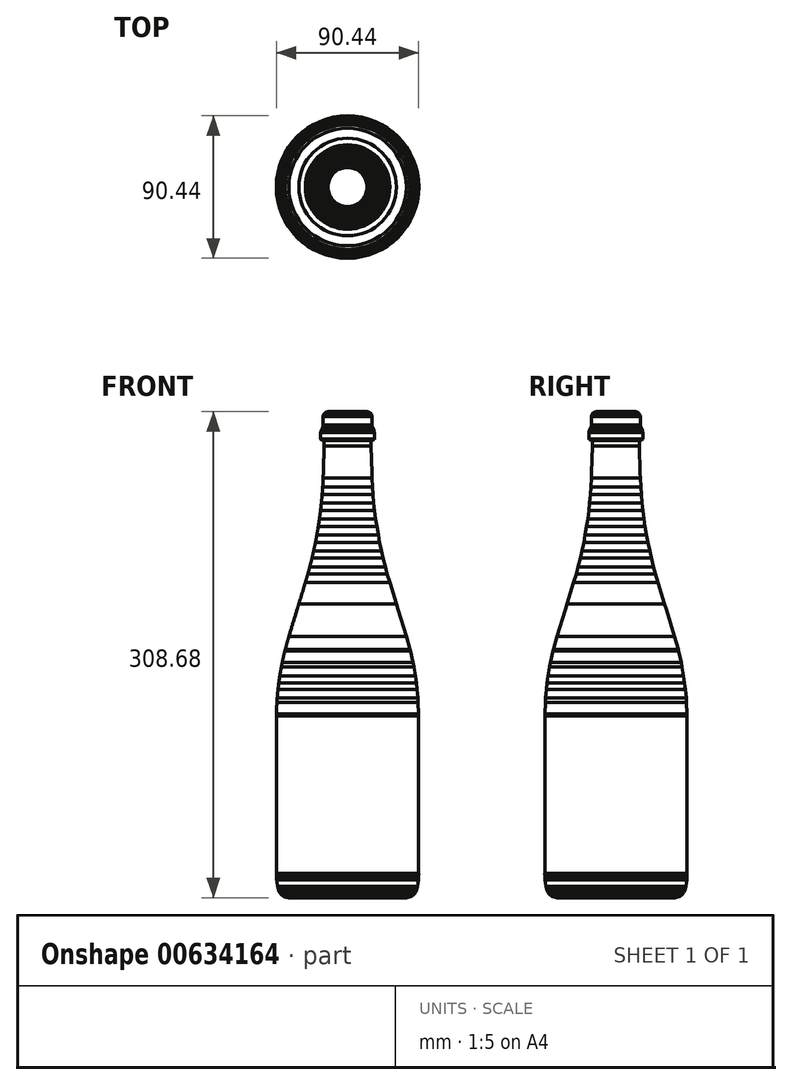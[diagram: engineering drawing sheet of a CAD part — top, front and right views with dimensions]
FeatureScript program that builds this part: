
annotation { "Feature Type Name" : "Feature", "Feature Type Description" : "" }
export const myFeature = defineFeature(function(context is Context, id is Id, definition is map)
    precondition{}
    {
        {
            var Q0;
            Q0=qCreatedBy(makeId("Front.planeOp"),FACE);
            var sketch = newSketch(context, id + "F0", { "sketchPlane" : qUnion([Q0])});
            skLineSegment(sketch, "E0", {"start": v(0, 154.34) * mm, "end": v(12.4, 154.34) * mm});
            skLineSegment(sketch, "E1", {"start": v(12.4, 154.34) * mm, "end": v(12.94, 154.29) * mm});
            skLineSegment(sketch, "E2", {"start": v(12.94, 154.29) * mm, "end": v(13.46, 154.15) * mm});
            skLineSegment(sketch, "E3", {"start": v(13.46, 154.15) * mm, "end": v(13.95, 153.92) * mm});
            skLineSegment(sketch, "E4", {"start": v(13.95, 153.92) * mm, "end": v(14.39, 153.62) * mm});
            skLineSegment(sketch, "E5", {"start": v(14.39, 153.62) * mm, "end": v(14.77, 153.24) * mm});
            skLineSegment(sketch, "E6", {"start": v(14.77, 153.24) * mm, "end": v(15.07, 152.8) * mm});
            skLineSegment(sketch, "E7", {"start": v(15.07, 152.8) * mm, "end": v(15.3, 152.31) * mm});
            skLineSegment(sketch, "E8", {"start": v(15.3, 152.31) * mm, "end": v(15.44, 151.8) * mm});
            skLineSegment(sketch, "E9", {"start": v(15.44, 151.8) * mm, "end": v(15.48, 151.26) * mm});
            skLineSegment(sketch, "E10", {"start": v(15.48, 151.26) * mm, "end": v(15.48, 145.78) * mm});
            skLineSegment(sketch, "E11", {"start": v(15.48, 145.78) * mm, "end": v(15.51, 145.34) * mm});
            skLineSegment(sketch, "E12", {"start": v(15.51, 145.34) * mm, "end": v(15.6, 144.9) * mm});
            skLineSegment(sketch, "E13", {"start": v(15.6, 144.9) * mm, "end": v(15.76, 144.5) * mm});
            skLineSegment(sketch, "E14", {"start": v(15.76, 144.5) * mm, "end": v(16.8, 142.26) * mm});
            skLineSegment(sketch, "E15", {"start": v(16.8, 142.26) * mm, "end": v(16.95, 141.85) * mm});
            skLineSegment(sketch, "E16", {"start": v(16.95, 141.85) * mm, "end": v(17.05, 141.42) * mm});
            skLineSegment(sketch, "E17", {"start": v(17.05, 141.42) * mm, "end": v(17.08, 140.98) * mm});
            skLineSegment(sketch, "E18", {"start": v(17.08, 140.98) * mm, "end": v(17.08, 137.14) * mm});
            skLineSegment(sketch, "E19", {"start": v(17.08, 137.14) * mm, "end": v(17.07, 137.03) * mm});
            skLineSegment(sketch, "E20", {"start": v(17.07, 137.03) * mm, "end": v(17.04, 136.93) * mm});
            skLineSegment(sketch, "E21", {"start": v(17.04, 136.93) * mm, "end": v(17, 136.83) * mm});
            skLineSegment(sketch, "E22", {"start": v(17, 136.83) * mm, "end": v(16.94, 136.74) * mm});
            skLineSegment(sketch, "E23", {"start": v(16.94, 136.74) * mm, "end": v(16.86, 136.67) * mm});
            skLineSegment(sketch, "E24", {"start": v(16.86, 136.67) * mm, "end": v(16.77, 136.6) * mm});
            skLineSegment(sketch, "E25", {"start": v(16.77, 136.6) * mm, "end": v(16.67, 136.56) * mm});
            skLineSegment(sketch, "E26", {"start": v(16.67, 136.56) * mm, "end": v(16.57, 136.53) * mm});
            skLineSegment(sketch, "E27", {"start": v(16.57, 136.53) * mm, "end": v(16.46, 136.52) * mm});
            skLineSegment(sketch, "E28", {"start": v(16.46, 136.52) * mm, "end": v(15.48, 136.52) * mm});
            skLineSegment(sketch, "E29", {"start": v(15.48, 136.52) * mm, "end": v(15.38, 136.51) * mm});
            skLineSegment(sketch, "E30", {"start": v(15.38, 136.51) * mm, "end": v(15.27, 136.49) * mm});
            skLineSegment(sketch, "E31", {"start": v(15.27, 136.49) * mm, "end": v(15.18, 136.44) * mm});
            skLineSegment(sketch, "E32", {"start": v(15.18, 136.44) * mm, "end": v(15.09, 136.38) * mm});
            skLineSegment(sketch, "E33", {"start": v(15.09, 136.38) * mm, "end": v(15.01, 136.3) * mm});
            skLineSegment(sketch, "E34", {"start": v(15.01, 136.3) * mm, "end": v(14.95, 136.22) * mm});
            skLineSegment(sketch, "E35", {"start": v(14.95, 136.22) * mm, "end": v(14.9, 136.12) * mm});
            skLineSegment(sketch, "E36", {"start": v(14.9, 136.12) * mm, "end": v(14.88, 136.01) * mm});
            skLineSegment(sketch, "E37", {"start": v(14.88, 136.01) * mm, "end": v(14.87, 135.9) * mm});
            skLineSegment(sketch, "E38", {"start": v(14.87, 135.9) * mm, "end": v(14.88, 132.5) * mm});
            skLineSegment(sketch, "E39", {"start": v(14.88, 132.5) * mm, "end": v(15.38, 115.37) * mm});
            skLineSegment(sketch, "E40", {"start": v(15.38, 115.37) * mm, "end": v(15.5, 112.14) * mm});
            skLineSegment(sketch, "E41", {"start": v(15.5, 112.14) * mm, "end": v(15.79, 106.54) * mm});
            skLineSegment(sketch, "E42", {"start": v(15.79, 106.54) * mm, "end": v(16.13, 101.76) * mm});
            skLineSegment(sketch, "E43", {"start": v(16.13, 101.76) * mm, "end": v(16.63, 96.29) * mm});
            skLineSegment(sketch, "E44", {"start": v(16.63, 96.29) * mm, "end": v(17.16, 91.56) * mm});
            skLineSegment(sketch, "E45", {"start": v(17.16, 91.56) * mm, "end": v(17.88, 86.07) * mm});
            skLineSegment(sketch, "E46", {"start": v(17.88, 86.07) * mm, "end": v(18.58, 81.4) * mm});
            skLineSegment(sketch, "E47", {"start": v(18.58, 81.4) * mm, "end": v(19.52, 75.9) * mm});
            skLineSegment(sketch, "E48", {"start": v(19.52, 75.9) * mm, "end": v(20.4, 71.3) * mm});
            skLineSegment(sketch, "E49", {"start": v(20.4, 71.3) * mm, "end": v(21.56, 65.79) * mm});
            skLineSegment(sketch, "E50", {"start": v(21.56, 65.79) * mm, "end": v(22.6, 61.3) * mm});
            skLineSegment(sketch, "E51", {"start": v(22.6, 61.3) * mm, "end": v(24, 55.76) * mm});
            skLineSegment(sketch, "E52", {"start": v(24, 55.76) * mm, "end": v(25.19, 51.37) * mm});
            skLineSegment(sketch, "E53", {"start": v(25.19, 51.37) * mm, "end": v(26.81, 45.85) * mm});
            skLineSegment(sketch, "E54", {"start": v(26.81, 45.85) * mm, "end": v(30.94, 32.33) * mm});
            skLineSegment(sketch, "E55", {"start": v(30.94, 32.33) * mm, "end": v(30.94, 32.32) * mm});
            skLineSegment(sketch, "E56", {"start": v(30.94, 32.32) * mm, "end": v(30.94, 32.32) * mm});
            skLineSegment(sketch, "E57", {"start": v(30.94, 32.32) * mm, "end": v(32.06, 28.67) * mm});
            skLineSegment(sketch, "E58", {"start": v(32.06, 28.67) * mm, "end": v(36.93, 12.71) * mm});
            skLineSegment(sketch, "E59", {"start": v(36.93, 12.71) * mm, "end": v(36.94, 12.7) * mm});
            skLineSegment(sketch, "E60", {"start": v(36.94, 12.7) * mm, "end": v(36.94, 12.7) * mm});
            skLineSegment(sketch, "E61", {"start": v(36.94, 12.7) * mm, "end": v(37.3, 11.5) * mm});
            skLineSegment(sketch, "E62", {"start": v(37.3, 11.5) * mm, "end": v(39.6, 3.28) * mm});
            skLineSegment(sketch, "E63", {"start": v(39.6, 3.28) * mm, "end": v(39.87, 2.25) * mm});
            skLineSegment(sketch, "E64", {"start": v(39.87, 2.25) * mm, "end": v(41.52, -5.05) * mm});
            skLineSegment(sketch, "E65", {"start": v(41.52, -5.05) * mm, "end": v(42.06, -7.77) * mm});
            skLineSegment(sketch, "E66", {"start": v(42.06, -7.77) * mm, "end": v(42.06, -7.77) * mm});
            skLineSegment(sketch, "E67", {"start": v(42.06, -7.77) * mm, "end": v(43.04, -13.46) * mm});
            skLineSegment(sketch, "E68", {"start": v(43.04, -13.46) * mm, "end": v(43.68, -17.9) * mm});
            skLineSegment(sketch, "E69", {"start": v(43.68, -17.9) * mm, "end": v(44.16, -21.92) * mm});
            skLineSegment(sketch, "E70", {"start": v(44.16, -21.92) * mm, "end": v(44.68, -27.48) * mm});
            skLineSegment(sketch, "E71", {"start": v(44.68, -27.48) * mm, "end": v(44.88, -30.41) * mm});
            skLineSegment(sketch, "E72", {"start": v(44.88, -30.41) * mm, "end": v(45.18, -37.72) * mm});
            skLineSegment(sketch, "E73", {"start": v(45.18, -37.72) * mm, "end": v(45.2, -38.92) * mm});
            skLineSegment(sketch, "E74", {"start": v(45.2, -38.92) * mm, "end": v(45.19, -138.95) * mm});
            skLineSegment(sketch, "E75", {"start": v(45.18, -140.89) * mm, "end": v(45.02, -143) * mm});
            skLineSegment(sketch, "E76", {"start": v(45.02, -143) * mm, "end": v(44.42, -147.02) * mm});
            skLineSegment(sketch, "E77", {"start": v(44.42, -147.02) * mm, "end": v(43.88, -149.36) * mm});
            skLineSegment(sketch, "E78", {"start": v(43.88, -149.36) * mm, "end": v(43.55, -150.32) * mm});
            skLineSegment(sketch, "E79", {"start": v(43.55, -150.32) * mm, "end": v(43.24, -150.94) * mm});
            skLineSegment(sketch, "E80", {"start": v(43.24, -150.94) * mm, "end": v(43.24, -150.94) * mm});
            skLineSegment(sketch, "E81", {"start": v(43.24, -150.94) * mm, "end": v(43.24, -150.95) * mm});
            skLineSegment(sketch, "E82", {"start": v(43.24, -150.95) * mm, "end": v(43.24, -150.95) * mm});
            skLineSegment(sketch, "E83", {"start": v(43.24, -150.95) * mm, "end": v(43, -151.33) * mm});
            skLineSegment(sketch, "E84", {"start": v(43, -151.33) * mm, "end": v(42.3, -152.22) * mm});
            skLineSegment(sketch, "E85", {"start": v(42.3, -152.22) * mm, "end": v(41.5, -152.95) * mm});
            skLineSegment(sketch, "E86", {"start": v(41.5, -152.95) * mm, "end": v(40.58, -153.55) * mm});
            skLineSegment(sketch, "E87", {"start": v(40.58, -153.55) * mm, "end": v(39.58, -153.98) * mm});
            skLineSegment(sketch, "E88", {"start": v(39.58, -153.98) * mm, "end": v(38.54, -154.24) * mm});
            skLineSegment(sketch, "E89", {"start": v(38.54, -154.24) * mm, "end": v(37.43, -154.34) * mm});
            skLineSegment(sketch, "E90", {"start": v(37.43, -154.34) * mm, "end": v(-37.43, -154.34) * mm});
            skLineSegment(sketch, "E91", {"start": v(-37.43, -154.34) * mm, "end": v(-38.54, -154.24) * mm});
            skLineSegment(sketch, "E92", {"start": v(-38.54, -154.24) * mm, "end": v(-39.58, -153.98) * mm});
            skLineSegment(sketch, "E93", {"start": v(-39.58, -153.98) * mm, "end": v(-40.58, -153.55) * mm});
            skLineSegment(sketch, "E94", {"start": v(-40.58, -153.55) * mm, "end": v(-41.5, -152.95) * mm});
            skLineSegment(sketch, "E95", {"start": v(-41.5, -152.95) * mm, "end": v(-42.3, -152.22) * mm});
            skLineSegment(sketch, "E96", {"start": v(-42.3, -152.22) * mm, "end": v(-43, -151.33) * mm});
            skLineSegment(sketch, "E97", {"start": v(-43, -151.33) * mm, "end": v(-43.24, -150.95) * mm});
            skLineSegment(sketch, "E98", {"start": v(-43.24, -150.95) * mm, "end": v(-43.24, -150.95) * mm});
            skLineSegment(sketch, "E99", {"start": v(-43.24, -150.95) * mm, "end": v(-43.24, -150.94) * mm});
            skLineSegment(sketch, "E100", {"start": v(-43.24, -150.94) * mm, "end": v(-43.24, -150.94) * mm});
            skLineSegment(sketch, "E101", {"start": v(-43.24, -150.94) * mm, "end": v(-43.55, -150.32) * mm});
            skLineSegment(sketch, "E102", {"start": v(-43.55, -150.32) * mm, "end": v(-43.88, -149.36) * mm});
            skLineSegment(sketch, "E103", {"start": v(-43.88, -149.36) * mm, "end": v(-44.42, -147.02) * mm});
            skLineSegment(sketch, "E104", {"start": v(-44.42, -147.02) * mm, "end": v(-45.02, -143) * mm});
            skLineSegment(sketch, "E105", {"start": v(-45.02, -143) * mm, "end": v(-45.18, -140.89) * mm});
            skLineSegment(sketch, "E106", {"start": v(-45.18, -140.89) * mm, "end": v(-45.2, -140.27) * mm});
            skLineSegment(sketch, "E107", {"start": v(-45.2, -140.27) * mm, "end": v(-45.22, -138.95) * mm});
            skLineSegment(sketch, "E108", {"start": v(-45.22, -138.95) * mm, "end": v(-45.2, -38.92) * mm});
            skLineSegment(sketch, "E109", {"start": v(-45.2, -38.92) * mm, "end": v(-45.18, -37.72) * mm});
            skLineSegment(sketch, "E110", {"start": v(-45.18, -37.72) * mm, "end": v(-44.88, -30.41) * mm});
            skLineSegment(sketch, "E111", {"start": v(-44.88, -30.41) * mm, "end": v(-44.68, -27.48) * mm});
            skLineSegment(sketch, "E112", {"start": v(-44.68, -27.48) * mm, "end": v(-44.16, -21.92) * mm});
            skLineSegment(sketch, "E113", {"start": v(-44.16, -21.92) * mm, "end": v(-43.68, -17.9) * mm});
            skLineSegment(sketch, "E114", {"start": v(-43.68, -17.9) * mm, "end": v(-43.04, -13.46) * mm});
            skLineSegment(sketch, "E115", {"start": v(-43.04, -13.46) * mm, "end": v(-42.06, -7.77) * mm});
            skLineSegment(sketch, "E116", {"start": v(-42.06, -7.77) * mm, "end": v(-41.52, -5.05) * mm});
            skLineSegment(sketch, "E117", {"start": v(-41.52, -5.05) * mm, "end": v(-39.87, 2.25) * mm});
            skLineSegment(sketch, "E118", {"start": v(-39.87, 2.25) * mm, "end": v(-39.6, 3.28) * mm});
            skLineSegment(sketch, "E119", {"start": v(-39.6, 3.28) * mm, "end": v(-37.3, 11.5) * mm});
            skLineSegment(sketch, "E120", {"start": v(-37.3, 11.5) * mm, "end": v(-32.06, 28.67) * mm});
            skLineSegment(sketch, "E121", {"start": v(-32.06, 28.67) * mm, "end": v(-30.94, 32.32) * mm});
            skLineSegment(sketch, "E122", {"start": v(-30.94, 32.32) * mm, "end": v(-30.94, 32.32) * mm});
            skLineSegment(sketch, "E123", {"start": v(-30.94, 32.32) * mm, "end": v(-30.94, 32.33) * mm});
            skLineSegment(sketch, "E124", {"start": v(-30.94, 32.33) * mm, "end": v(-26.81, 45.85) * mm});
            skLineSegment(sketch, "E125", {"start": v(-26.81, 45.85) * mm, "end": v(-25.19, 51.37) * mm});
            skLineSegment(sketch, "E126", {"start": v(-25.19, 51.37) * mm, "end": v(-24, 55.76) * mm});
            skLineSegment(sketch, "E127", {"start": v(-24, 55.76) * mm, "end": v(-22.6, 61.3) * mm});
            skLineSegment(sketch, "E128", {"start": v(-22.6, 61.3) * mm, "end": v(-21.56, 65.79) * mm});
            skLineSegment(sketch, "E129", {"start": v(-21.56, 65.79) * mm, "end": v(-20.4, 71.3) * mm});
            skLineSegment(sketch, "E130", {"start": v(-20.4, 71.3) * mm, "end": v(-19.52, 75.9) * mm});
            skLineSegment(sketch, "E131", {"start": v(-19.52, 75.9) * mm, "end": v(-18.58, 81.4) * mm});
            skLineSegment(sketch, "E132", {"start": v(-18.58, 81.4) * mm, "end": v(-17.88, 86.07) * mm});
            skLineSegment(sketch, "E133", {"start": v(-17.88, 86.07) * mm, "end": v(-17.16, 91.56) * mm});
            skLineSegment(sketch, "E134", {"start": v(-17.16, 91.56) * mm, "end": v(-16.63, 96.29) * mm});
            skLineSegment(sketch, "E135", {"start": v(-16.63, 96.29) * mm, "end": v(-16.13, 101.76) * mm});
            skLineSegment(sketch, "E136", {"start": v(-16.13, 101.76) * mm, "end": v(-15.79, 106.54) * mm});
            skLineSegment(sketch, "E137", {"start": v(-15.79, 106.54) * mm, "end": v(-15.5, 112.14) * mm});
            skLineSegment(sketch, "E138", {"start": v(-15.5, 112.14) * mm, "end": v(-15.38, 115.37) * mm});
            skLineSegment(sketch, "E139", {"start": v(-15.38, 115.37) * mm, "end": v(-14.88, 132.5) * mm});
            skLineSegment(sketch, "E140", {"start": v(-14.88, 132.5) * mm, "end": v(-14.87, 135.9) * mm});
            skLineSegment(sketch, "E141", {"start": v(-14.87, 135.9) * mm, "end": v(-14.88, 136.01) * mm});
            skLineSegment(sketch, "E142", {"start": v(-14.88, 136.01) * mm, "end": v(-14.9, 136.12) * mm});
            skLineSegment(sketch, "E143", {"start": v(-14.9, 136.12) * mm, "end": v(-14.95, 136.22) * mm});
            skLineSegment(sketch, "E144", {"start": v(-14.95, 136.22) * mm, "end": v(-15.01, 136.3) * mm});
            skLineSegment(sketch, "E145", {"start": v(-15.01, 136.3) * mm, "end": v(-15.09, 136.38) * mm});
            skLineSegment(sketch, "E146", {"start": v(-15.09, 136.38) * mm, "end": v(-15.18, 136.44) * mm});
            skLineSegment(sketch, "E147", {"start": v(-15.18, 136.44) * mm, "end": v(-15.27, 136.49) * mm});
            skLineSegment(sketch, "E148", {"start": v(-15.27, 136.49) * mm, "end": v(-15.38, 136.51) * mm});
            skLineSegment(sketch, "E149", {"start": v(-15.38, 136.51) * mm, "end": v(-15.48, 136.52) * mm});
            skLineSegment(sketch, "E150", {"start": v(-15.48, 136.52) * mm, "end": v(-16.46, 136.52) * mm});
            skLineSegment(sketch, "E151", {"start": v(-16.46, 136.52) * mm, "end": v(-16.57, 136.53) * mm});
            skLineSegment(sketch, "E152", {"start": v(-16.57, 136.53) * mm, "end": v(-16.67, 136.56) * mm});
            skLineSegment(sketch, "E153", {"start": v(-16.67, 136.56) * mm, "end": v(-16.77, 136.6) * mm});
            skLineSegment(sketch, "E154", {"start": v(-16.77, 136.6) * mm, "end": v(-16.86, 136.67) * mm});
            skLineSegment(sketch, "E155", {"start": v(-16.86, 136.67) * mm, "end": v(-16.94, 136.74) * mm});
            skLineSegment(sketch, "E156", {"start": v(-16.94, 136.74) * mm, "end": v(-17, 136.83) * mm});
            skLineSegment(sketch, "E157", {"start": v(-17, 136.83) * mm, "end": v(-17.04, 136.93) * mm});
            skLineSegment(sketch, "E158", {"start": v(-17.04, 136.93) * mm, "end": v(-17.07, 137.03) * mm});
            skLineSegment(sketch, "E159", {"start": v(-17.07, 137.03) * mm, "end": v(-17.08, 137.14) * mm});
            skLineSegment(sketch, "E160", {"start": v(-17.08, 137.14) * mm, "end": v(-17.08, 140.98) * mm});
            skLineSegment(sketch, "E161", {"start": v(-17.08, 140.98) * mm, "end": v(-17.05, 141.42) * mm});
            skLineSegment(sketch, "E162", {"start": v(-17.05, 141.42) * mm, "end": v(-16.95, 141.85) * mm});
            skLineSegment(sketch, "E163", {"start": v(-16.95, 141.85) * mm, "end": v(-16.8, 142.26) * mm});
            skLineSegment(sketch, "E164", {"start": v(-16.8, 142.26) * mm, "end": v(-15.76, 144.5) * mm});
            skLineSegment(sketch, "E165", {"start": v(-15.76, 144.5) * mm, "end": v(-15.6, 144.9) * mm});
            skLineSegment(sketch, "E166", {"start": v(-15.6, 144.9) * mm, "end": v(-15.51, 145.34) * mm});
            skLineSegment(sketch, "E167", {"start": v(-15.51, 145.34) * mm, "end": v(-15.48, 145.78) * mm});
            skLineSegment(sketch, "E168", {"start": v(-15.48, 145.78) * mm, "end": v(-15.48, 151.26) * mm});
            skLineSegment(sketch, "E169", {"start": v(-15.48, 151.26) * mm, "end": v(-15.44, 151.8) * mm});
            skLineSegment(sketch, "E170", {"start": v(-15.44, 151.8) * mm, "end": v(-15.3, 152.31) * mm});
            skLineSegment(sketch, "E171", {"start": v(-15.3, 152.31) * mm, "end": v(-15.07, 152.8) * mm});
            skLineSegment(sketch, "E172", {"start": v(-15.07, 152.8) * mm, "end": v(-14.77, 153.24) * mm});
            skLineSegment(sketch, "E173", {"start": v(-14.77, 153.24) * mm, "end": v(-14.39, 153.62) * mm});
            skLineSegment(sketch, "E174", {"start": v(-14.39, 153.62) * mm, "end": v(-13.95, 153.92) * mm});
            skLineSegment(sketch, "E175", {"start": v(-13.95, 153.92) * mm, "end": v(-13.46, 154.15) * mm});
            skLineSegment(sketch, "E176", {"start": v(-13.46, 154.15) * mm, "end": v(-12.94, 154.29) * mm});
            skLineSegment(sketch, "E177", {"start": v(-12.94, 154.29) * mm, "end": v(-12.4, 154.34) * mm});
            skLineSegment(sketch, "E178", {"start": v(-12.4, 154.34) * mm, "end": v(0, 154.34) * mm});
            skLineSegment(sketch, "E179", {"start": v(45.19, -138.95) * mm, "end": v(45.18, -140.89) * mm});
            skLineSegment(sketch, "E180", {"start": v(0, 176.34) * mm, "end": v(0, -209) * mm, "construction": true});
            skPoint(sketch, "E180.endSnap0", {"position": v(0, -154.34) * mm});
            skSolve(sketch);
        }
        {
            var Q0;
            Q0=sQuery(id+"F0.wireOp",EDGE,"E74");
            var Q1;
            Q1=sQuery(id+"F0.wireOp",EDGE,"E120");
            var Q2;
            Q2=sQuery(id+"F0.wireOp",EDGE,"E139");
            var Q3;
            Q3=sQuery(id+"F0.wireOp",EDGE,"E137");
            var Q4;
            Q4=sQuery(id+"F0.wireOp",EDGE,"E135");
            var Q5;
            Q5=sQuery(id+"F0.wireOp",EDGE,"E128");
            var Q6;
            Q6=sQuery(id+"F0.wireOp",EDGE,"E132");
            var Q7;
            Q7=sQuery(id+"F0.wireOp",EDGE,"E131");
            var Q8;
            Q8=sQuery(id+"F0.wireOp",EDGE,"E130");
            var Q9;
            Q9=sQuery(id+"F0.wireOp",EDGE,"E129");
            var Q10;
            Q10=sQuery(id+"F0.wireOp",EDGE,"E134");
            var Q11;
            Q11=sQuery(id+"F0.wireOp",EDGE,"E133");
            var Q12;
            Q12=sQuery(id+"F0.wireOp",EDGE,"E136");
            var Q13;
            Q13=sQuery(id+"F0.wireOp",EDGE,"E138");
            var Q14;
            Q14=sQuery(id+"F0.wireOp",EDGE,"E140");
            var Q15;
            Q15=sQuery(id+"F0.wireOp",EDGE,"E160");
            var Q16;
            Q16=sQuery(id+"F0.wireOp",EDGE,"E168");
            var Q17;
            Q17=sQuery(id+"F0.wireOp",EDGE,"E172");
            var Q18;
            Q18=sQuery(id+"F0.wireOp",EDGE,"E169");
            var Q19;
            Q19=sQuery(id+"F0.wireOp",EDGE,"E174");
            var Q20;
            Q20=sQuery(id+"F0.wireOp",EDGE,"E170");
            var Q21;
            Q21=sQuery(id+"F0.wireOp",EDGE,"E175");
            var Q22;
            Q22=sQuery(id+"F0.wireOp",EDGE,"E176");
            var Q23;
            Q23=sQuery(id+"F0.wireOp",EDGE,"E173");
            var Q24;
            Q24=sQuery(id+"F0.wireOp",EDGE,"E165");
            var Q25;
            Q25=sQuery(id+"F0.wireOp",EDGE,"E163");
            var Q26;
            Q26=sQuery(id+"F0.wireOp",EDGE,"E167");
            var Q27;
            Q27=sQuery(id+"F0.wireOp",EDGE,"E164");
            var Q28;
            Q28=sQuery(id+"F0.wireOp",EDGE,"E162");
            var Q29;
            Q29=sQuery(id+"F0.wireOp",EDGE,"E177");
            var Q30;
            Q30=sQuery(id+"F0.wireOp",EDGE,"E171");
            var Q31;
            Q31=sQuery(id+"F0.wireOp",EDGE,"E166");
            var Q32;
            Q32=sQuery(id+"F0.wireOp",EDGE,"E161");
            var Q33;
            Q33=sQuery(id+"F0.wireOp",EDGE,"E142");
            var Q34;
            Q34=sQuery(id+"F0.wireOp",EDGE,"E150");
            var Q35;
            Q35=sQuery(id+"F0.wireOp",EDGE,"E144");
            var Q36;
            Q36=sQuery(id+"F0.wireOp",EDGE,"E143");
            var Q37;
            Q37=sQuery(id+"F0.wireOp",EDGE,"E141");
            var Q38;
            Q38=sQuery(id+"F0.wireOp",EDGE,"E149");
            var Q39;
            Q39=sQuery(id+"F0.wireOp",EDGE,"E148");
            var Q40;
            Q40=sQuery(id+"F0.wireOp",EDGE,"E145");
            var Q41;
            Q41=sQuery(id+"F0.wireOp",EDGE,"E147");
            var Q42;
            Q42=sQuery(id+"F0.wireOp",EDGE,"E159");
            var Q43;
            Q43=sQuery(id+"F0.wireOp",EDGE,"E156");
            var Q44;
            Q44=sQuery(id+"F0.wireOp",EDGE,"E157");
            var Q45;
            Q45=sQuery(id+"F0.wireOp",EDGE,"E151");
            var Q46;
            Q46=sQuery(id+"F0.wireOp",EDGE,"E146");
            var Q47;
            Q47=sQuery(id+"F0.wireOp",EDGE,"E158");
            var Q48;
            Q48=sQuery(id+"F0.wireOp",EDGE,"E154");
            var Q49;
            Q49=sQuery(id+"F0.wireOp",EDGE,"E155");
            var Q50;
            Q50=sQuery(id+"F0.wireOp",EDGE,"E153");
            var Q51;
            Q51=sQuery(id+"F0.wireOp",EDGE,"E152");
            var Q52;
            Q52=sQuery(id+"F0.wireOp",EDGE,"E124");
            var Q53;
            Q53=sQuery(id+"F0.wireOp",EDGE,"E127");
            var Q54;
            Q54=sQuery(id+"F0.wireOp",EDGE,"E125");
            var Q55;
            Q55=sQuery(id+"F0.wireOp",EDGE,"E126");
            var Q56;
            Q56=sQuery(id+"F0.wireOp",EDGE,"E121");
            var Q57;
            Q57=sQuery(id+"F0.wireOp",EDGE,"E122");
            var Q58;
            Q58=sQuery(id+"F0.wireOp",EDGE,"E123");
            var Q59;
            Q59=sQuery(id+"F0.wireOp",EDGE,"E119");
            var Q60;
            Q60=sQuery(id+"F0.wireOp",EDGE,"E109");
            var Q61;
            Q61=sQuery(id+"F0.wireOp",EDGE,"E110");
            var Q62;
            Q62=sQuery(id+"F0.wireOp",EDGE,"E111");
            var Q63;
            Q63=sQuery(id+"F0.wireOp",EDGE,"E112");
            var Q64;
            Q64=sQuery(id+"F0.wireOp",EDGE,"E117");
            var Q65;
            Q65=sQuery(id+"F0.wireOp",EDGE,"E115");
            var Q66;
            Q66=sQuery(id+"F0.wireOp",EDGE,"E113");
            var Q67;
            Q67=sQuery(id+"F0.wireOp",EDGE,"E116");
            var Q68;
            Q68=sQuery(id+"F0.wireOp",EDGE,"E114");
            var Q69;
            Q69=sQuery(id+"F0.wireOp",EDGE,"E118");
            var Q70;
            Q70=sQuery(id+"F0.wireOp",EDGE,"E104");
            var Q71;
            Q71=sQuery(id+"F0.wireOp",EDGE,"E107");
            var Q72;
            Q72=sQuery(id+"F0.wireOp",EDGE,"E92");
            var Q73;
            Q73=sQuery(id+"F0.wireOp",EDGE,"E91");
            var Q74;
            Q74=sQuery(id+"F0.wireOp",EDGE,"E106");
            var Q75;
            Q75=sQuery(id+"F0.wireOp",EDGE,"E95");
            var Q76;
            Q76=sQuery(id+"F0.wireOp",EDGE,"E102");
            var Q77;
            Q77=sQuery(id+"F0.wireOp",EDGE,"E93");
            var Q78;
            Q78=sQuery(id+"F0.wireOp",EDGE,"E96");
            var Q79;
            Q79=sQuery(id+"F0.wireOp",EDGE,"E94");
            var Q80;
            Q80=sQuery(id+"F0.wireOp",EDGE,"E105");
            var Q81;
            Q81=sQuery(id+"F0.wireOp",EDGE,"E103");
            var Q82;
            Q82=sQuery(id+"F0.wireOp",EDGE,"E97");
            var Q83;
            Q83=sQuery(id+"F0.wireOp",EDGE,"E101");
            var Q84;
            Q84=sQuery(id+"F0.wireOp",EDGE,"E100");
            var Q85;
            Q85=sQuery(id+"F0.wireOp",EDGE,"E100");
            var Q86;
            Q86=sQuery(id+"F0.wireOp",EDGE,"E99");
            var Q87;
            Q87=sQuery(id+"F0.wireOp",EDGE,"E98");
            var Q88;
            Q88=sQuery(id+"F0.wireOp",EDGE,"E180");
            revolve(context, id + "F1", {"bodyType" : ToolBodyType.SURFACE, "operationType" : NewBodyOperationType.ADD, "surfaceEntities" : qUnion([Q0, Q1, Q2, Q3, Q4, Q5, Q6, Q7, Q8, Q9, Q10, Q11, Q12, Q13, Q14, Q15, Q16, Q17, Q18, Q19, Q20, Q21, Q22, Q23, Q24, Q25, Q26, Q27, Q28, Q29, Q30, Q31, Q32, Q33, Q34, Q35, Q36, Q37, Q38, Q39, Q40, Q41, Q42, Q43, Q44, Q45, Q46, Q47, Q48, Q49, Q50, Q51, Q52, Q53, Q54, Q55, Q56, Q57, Q58, Q59, Q60, Q61, Q62, Q63, Q64, Q65, Q66, Q67, Q68, Q69, Q70, Q71, Q72, Q73, Q74, Q75, Q76, Q77, Q78, Q79, Q80, Q81, Q82, Q83, Q84, Q85, Q86, Q87]), "axis" : qUnion([Q88]), "revolveType" : RevolveType.FULL});
        }
    });
